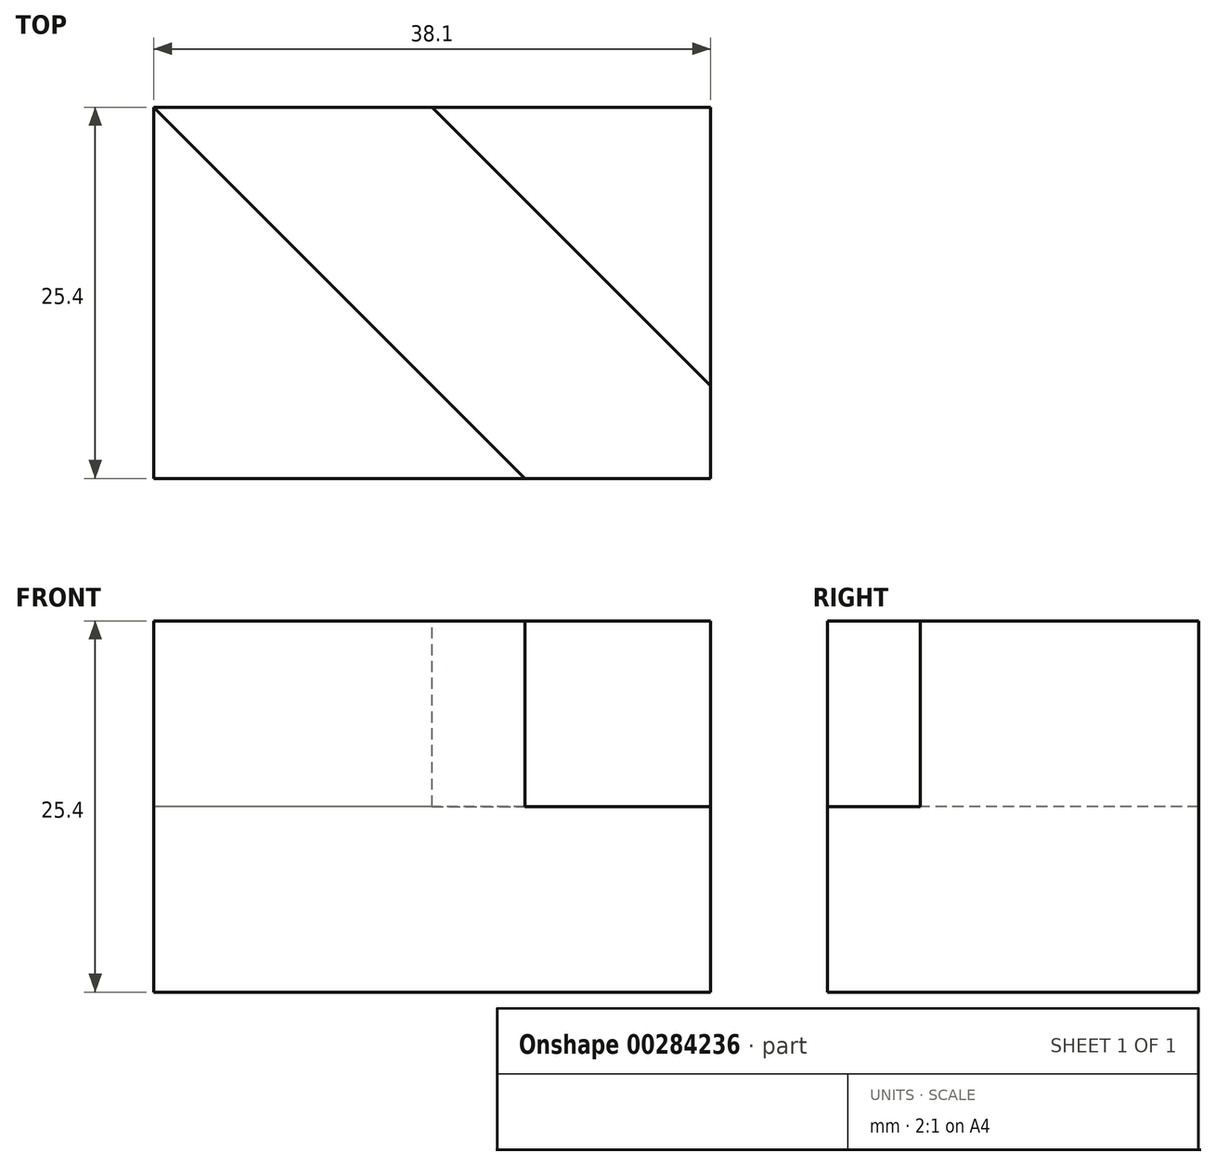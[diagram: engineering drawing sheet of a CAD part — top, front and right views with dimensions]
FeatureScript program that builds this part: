
annotation { "Feature Type Name" : "Feature", "Feature Type Description" : "" }
export const myFeature = defineFeature(function(context is Context, id is Id, definition is map)
    precondition{}
    {
        {
            var Q0;
            Q0=qCreatedBy(makeId("Front.planeOp"),FACE);
            var sketch = newSketch(context, id + "F0", { "sketchPlane" : qUnion([Q0])});
            skLineSegment(sketch, "E0", {"start": v(0, 25.4) * mm, "end": v(0, 0) * mm});
            skLineSegment(sketch, "E1", {"start": v(0, 0) * mm, "end": v(38.1, 0) * mm});
            skLineSegment(sketch, "E2", {"start": v(38.1, 0) * mm, "end": v(38.1, 25.4) * mm});
            skLineSegment(sketch, "E3", {"start": v(38.1, 25.4) * mm, "end": v(0, 25.4) * mm});
            skSolve(sketch);
        }
        {
            var Q0;
            Q0 = qSketchRegion(id + "F0", true);
            extrude(context, id + "F1", {"entities" : qUnion([Q0]), "endBound" : BoundingType.SYMMETRIC, "depth" : 25.4 * mm});
        }
        {
            var Q0;
            Q0=makeQuery(id+"F1.opExtrude","SWEPT_FACE",FACE,{"disambiguationData":[OSD([sQuery(id+"F0.wireOp",EDGE,"E2")])]});
            var sketch = newSketch(context, id + "F2", { "sketchPlane" : qUnion([Q0])});
            skLineSegment(sketch, "E4.bottom", {"start": v(-12.7, 25.4) * mm, "end": v(-6.35, 25.4) * mm});
            skLineSegment(sketch, "E4.top", {"start": v(-12.7, 12.7) * mm, "end": v(-6.35, 12.7) * mm});
            skLineSegment(sketch, "E4.left", {"start": v(-12.7, 25.4) * mm, "end": v(-12.7, 12.7) * mm});
            skLineSegment(sketch, "E4.right", {"start": v(-6.35, 25.4) * mm, "end": v(-6.35, 12.7) * mm});
            skSolve(sketch);
        }
        {
            var Q0;
            Q0=makeQuery(id+"F2.imprint","IMPRINT",FACE,{"disambiguationData":[TD([[makeQuery(id+"F2.imprint","IMPRINT",EDGE,{"derivedFrom":sQuery(id+"F2.wireOp",EDGE,"E4.bottom")}),-1.0]])]});
            extrude(context, id + "F3", {"entities" : qUnion([Q0]), "operationType" : NewBodyOperationType.REMOVE, "oppositeDirection" : true, "depth" : 12.7 * mm});
        }
        {
            var Q0;
            Q0=makeQuery(id+"F1.opExtrude","SWEPT_FACE",FACE,{"disambiguationData":[OSD([sQuery(id+"F0.wireOp",EDGE,"E3")])]});
            var sketch = newSketch(context, id + "F4", { "sketchPlane" : qUnion([Q0])});
            skLineSegment(sketch, "E5", {"start": v(25.4, -12.7) * mm, "end": v(0, 12.7) * mm});
            skLineSegment(sketch, "E6", {"start": v(0, 12.7) * mm, "end": v(19.05, 12.7) * mm});
            skLineSegment(sketch, "E7", {"start": v(19.05, 12.7) * mm, "end": v(38.1, -6.35) * mm});
            skLineSegment(sketch, "E8", {"start": v(38.1, -6.35) * mm, "end": v(25.4, -6.35) * mm});
            skLineSegment(sketch, "E9", {"start": v(25.4, -6.35) * mm, "end": v(25.4, -12.7) * mm});
            skSolve(sketch);
        }
        {
            var Q0;
            Q0=makeQuery(id+"F4.imprint","IMPRINT",FACE,{"disambiguationData":[TD([[makeQuery(id+"F4.imprint","IMPRINT",EDGE,{"derivedFrom":sQuery(id+"F4.wireOp",EDGE,"E5")}),-1.0]])]});
            extrude(context, id + "F5", {"entities" : qUnion([Q0]), "operationType" : NewBodyOperationType.REMOVE, "oppositeDirection" : true, "depth" : 12.7 * mm});
        }
    });
